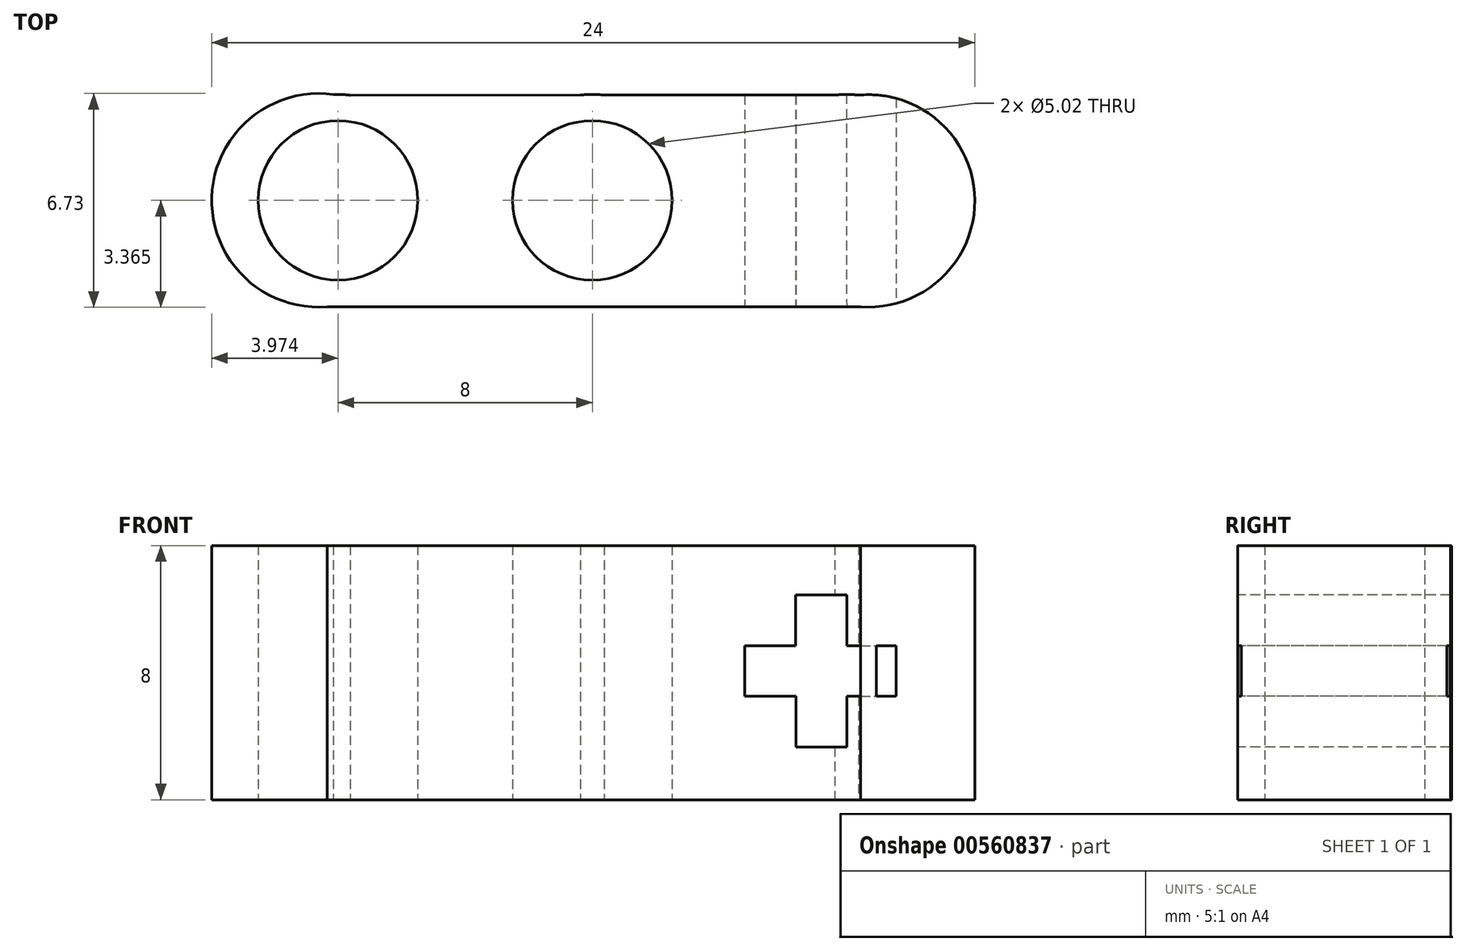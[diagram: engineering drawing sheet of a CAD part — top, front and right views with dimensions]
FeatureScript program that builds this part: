
annotation { "Feature Type Name" : "Feature", "Feature Type Description" : "" }
export const myFeature = defineFeature(function(context is Context, id is Id, definition is map)
    precondition{}
    {
        {
            var Q0;
            Q0=qCreatedBy(makeId("Top.planeOp"),FACE);
            var sketch = newSketch(context, id + "F0", { "sketchPlane" : qUnion([Q0])});
            skArc(sketch, "E0", {"start": v(8.4, -3.35) * mm, "mid": v(12, 0) * mm, "end": v(8.36, 3.3) * mm});
            skArc(sketch, "E1", {"start": v(-8.06, 3.3) * mm, "mid": v(-12, 0.16) * mm, "end": v(-8.38, -3.36) * mm});
            skLineSegment(sketch, "E2", {"start": v(-8.06, 3.3) * mm, "end": v(8.36, 3.3) * mm});
            skLineSegment(sketch, "E3", {"start": v(-8.38, -3.36) * mm, "end": v(8.4, -3.35) * mm});
            skCircle(sketch, "E4.1.0.1", {"center": v(7.96, 0) * mm, "radius": 3.33 * mm});
            skCircle(sketch, "E4.2.0.0", {"center": v(-0.04, 0) * mm, "radius": 2.5 * mm});
            skCircle(sketch, "E4.2.0.1", {"center": v(-0.04, 0) * mm, "radius": 3.33 * mm});
            skCircle(sketch, "E4.3.0.0", {"center": v(-8.04, 0) * mm, "radius": 2.5 * mm});
            skCircle(sketch, "E4.3.0.1", {"center": v(-8.04, 0) * mm, "radius": 3.33 * mm});
            skSolve(sketch);
        }
        {
            var Q0;
            Q0 = qSketchRegion(id + "F0", true);
            extrude(context, id + "F1", {"entities" : qUnion([Q0]), "depth" : 8 * mm, "offsetDistance" : 25.4 * mm});
        }
        {
            var Q0;
            Q0=makeQuery(id+"F1.opExtrude","SWEPT_FACE",FACE,{"disambiguationData":[OSD([sQuery(id+"F0.wireOp",EDGE,"E3")])]});
            var sketch = newSketch(context, id + "F2", { "sketchPlane" : qUnion([Q0])});
            skLineSegment(sketch, "E5", {"start": v(4.75, 4.84) * mm, "end": v(9.52, 4.84) * mm});
            skLineSegment(sketch, "E6", {"start": v(4.75, 3.25) * mm, "end": v(9.52, 3.25) * mm});
            skLineSegment(sketch, "E7", {"start": v(4.75, 4.84) * mm, "end": v(4.75, 3.25) * mm});
            skLineSegment(sketch, "E8", {"start": v(9.52, 4.84) * mm, "end": v(9.52, 3.25) * mm});
            skLineSegment(sketch, "E9", {"start": v(6.35, 4.84) * mm, "end": v(4.75, 4.84) * mm});
            skLineSegment(sketch, "E10", {"start": v(9.52, 4.84) * mm, "end": v(7.92, 4.84) * mm});
            skLineSegment(sketch, "E11", {"start": v(6.35, 4.84) * mm, "end": v(6.35, 6.45) * mm});
            skLineSegment(sketch, "E12", {"start": v(6.35, 6.45) * mm, "end": v(7.96, 6.45) * mm});
            skLineSegment(sketch, "E13", {"start": v(7.96, 6.45) * mm, "end": v(7.96, 4.84) * mm});
            skLineSegment(sketch, "E14", {"start": v(7.96, 5.05) * mm, "end": v(7.96, 4.84) * mm});
            skLineSegment(sketch, "E15", {"start": v(7.96, 5.05) * mm, "end": v(7.96, 1.66) * mm});
            skLineSegment(sketch, "E16", {"start": v(7.96, 1.66) * mm, "end": v(6.36, 1.66) * mm});
            skLineSegment(sketch, "E17", {"start": v(6.36, 1.66) * mm, "end": v(6.36, 5.05) * mm});
            skSolve(sketch);
        }
        {
            var Q0;
            Q0 = qSketchRegion(id + "F2", true);
            extrude(context, id + "F3", {"entities" : qUnion([Q0]), "operationType" : NewBodyOperationType.REMOVE, "depth" : -838.2 * mm, "offsetDistance" : 25.4 * mm});
        }
    });
